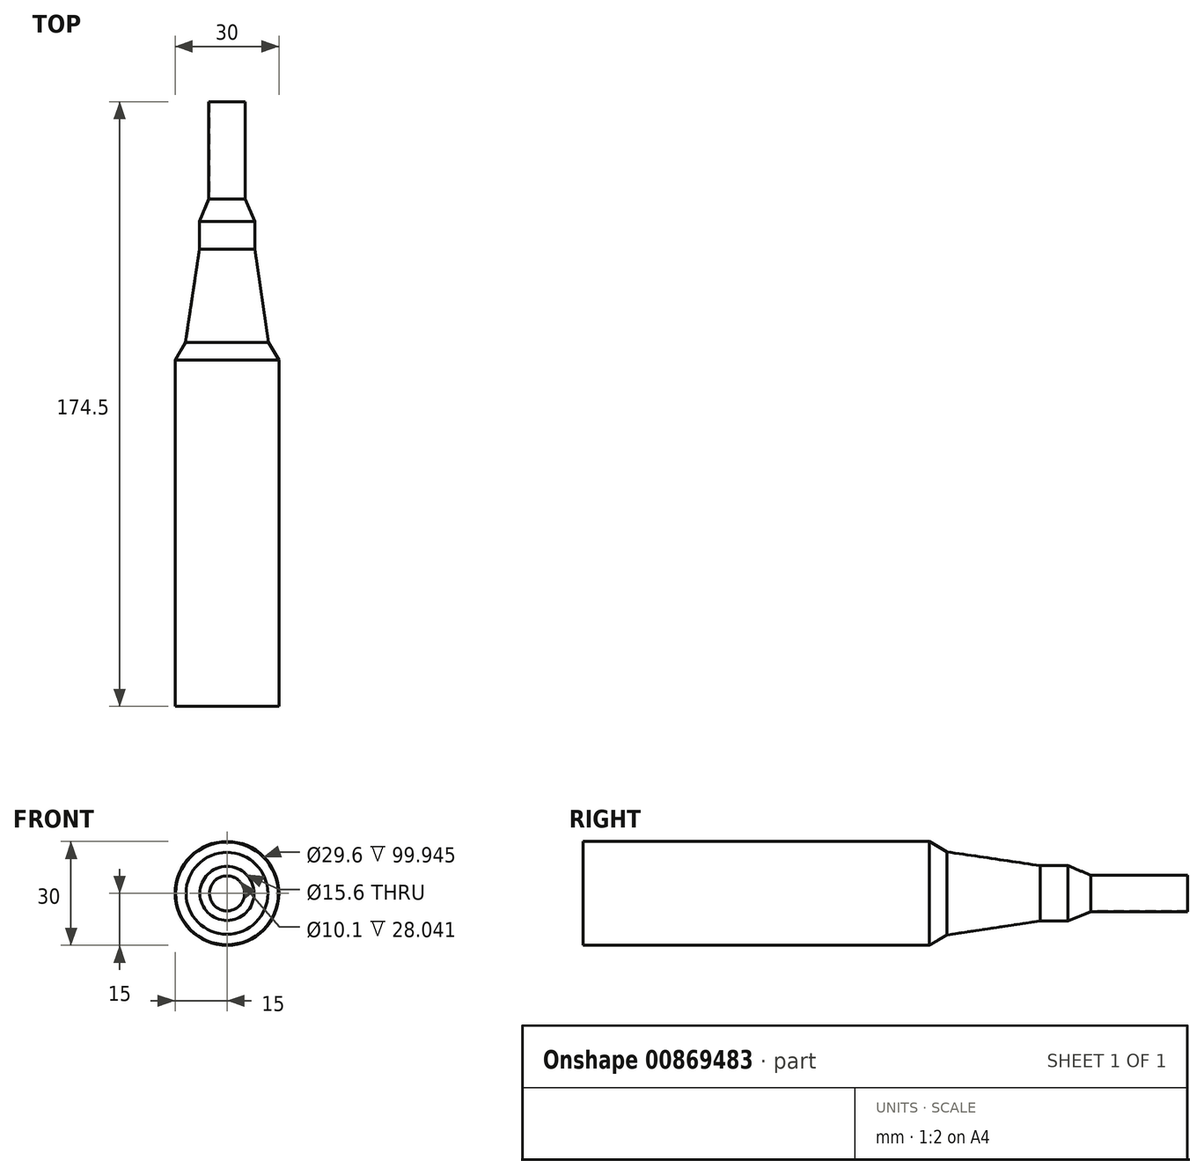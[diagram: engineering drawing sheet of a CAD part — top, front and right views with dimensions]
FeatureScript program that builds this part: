
annotation { "Feature Type Name" : "Feature", "Feature Type Description" : "" }
export const myFeature = defineFeature(function(context is Context, id is Id, definition is map)
    precondition{}
    {
        {
            var Q0;
            Q0=qCreatedBy(makeId("Front.planeOp"),FACE);
            var sketch = newSketch(context, id + "F0", { "sketchPlane" : qUnion([Q0])});
            skCircle(sketch, "E0", {"center": v(0, 0) * mm, "radius": 15 * mm});
            skSolve(sketch);
        }
        {
            var Q0;
            Q0=makeQuery(id+"F0.imprint","IMPRINT",FACE,{"disambiguationData":[TD([[makeQuery(id+"F0.imprint","IMPRINT",EDGE,{"derivedFrom":sQuery(id+"F0.wireOp",EDGE,"E0")}),1.0]])]});
            extrude(context, id + "F1", {"entities" : qUnion([Q0]), "oppositeDirection" : true, "depth" : 100 * mm, "offsetDistance" : 25 * mm});
        }
        {
            var Q0;
            Q0=makeQuery(id+"F1.opExtrude","CAP_FACE",FACE,{"disambiguationData":[OSD([sQuery(id+"F0.wireOp",EDGE,"E0")])],"isStart":false});
            cPlane(context, id + "F2", {"entities" : qUnion([Q0]), "cplaneType" : CPlaneType.OFFSET, "offset" : 5 * mm, "width" : 150 * mm, "height" : 150 * mm});
        }
        {
            var Q0;
            Q0=qCreatedBy(id+"F2.planeOp",FACE);
            var sketch = newSketch(context, id + "F3", { "sketchPlane" : qUnion([Q0])});
            skPoint(sketch, "E1.0", {"position": v(0, 0) * mm});
            skCircle(sketch, "E2", {"center": v(0, 0) * mm, "radius": 12 * mm});
            skSolve(sketch);
        }
        {
            var Q1;
            Q1=makeQuery(id+"F1.opExtrude","CAP_FACE",FACE,{"disambiguationData":[OSD([sQuery(id+"F0.wireOp",EDGE,"E0")])],"isStart":false});
            var Q2;
            Q2=makeQuery(id+"F3.imprint","IMPRINT",FACE,{"disambiguationData":[TD([[makeQuery(id+"F3.imprint","IMPRINT",EDGE,{"derivedFrom":sQuery(id+"F3.wireOp",EDGE,"E2")}),1.0]])]});
            loft(context, id + "F4", {"operationType" : NewBodyOperationType.ADD, "sheetProfilesArray" : [{ "sheetProfileEntities" : qUnion([Q1]) }, { "sheetProfileEntities" : qUnion([Q2]) }]});
        }
        {
            var Q0;
            Q0=makeQuery(id+"F4.opLoft","CAP_FACE",FACE,{"disambiguationData":[OSD([makeQuery(id+"F3.imprint","IMPRINT",FACE,{"disambiguationData":[TD([[makeQuery(id+"F3.imprint","IMPRINT",EDGE,{"derivedFrom":sQuery(id+"F3.wireOp",EDGE,"E2")}),1.0]])]})])],"isStart":true});
            cPlane(context, id + "F5", {"entities" : qUnion([Q0]), "cplaneType" : CPlaneType.OFFSET, "offset" : 27 * mm, "width" : 150 * mm, "height" : 150 * mm});
        }
        {
            var Q0;
            Q0=qCreatedBy(id+"F5.planeOp",FACE);
            var sketch = newSketch(context, id + "F6", { "sketchPlane" : qUnion([Q0])});
            skPoint(sketch, "E3.0", {"position": v(0, 0) * mm});
            skCircle(sketch, "E4", {"center": v(0, 0) * mm, "radius": 8 * mm});
            skSolve(sketch);
        }
        {
            var Q1;
            Q1=makeQuery(id+"F6.imprint","IMPRINT",FACE,{"disambiguationData":[TD([[makeQuery(id+"F6.imprint","IMPRINT",EDGE,{"derivedFrom":sQuery(id+"F6.wireOp",EDGE,"E4")}),1.0]])]});
            var Q2;
            Q2=makeQuery(id+"F4.opLoft","CAP_FACE",FACE,{"disambiguationData":[OSD([makeQuery(id+"F3.imprint","IMPRINT",FACE,{"disambiguationData":[TD([[makeQuery(id+"F3.imprint","IMPRINT",EDGE,{"derivedFrom":sQuery(id+"F3.wireOp",EDGE,"E2")}),1.0]])]})])],"isStart":true});
            loft(context, id + "F7", {"operationType" : NewBodyOperationType.ADD, "sheetProfilesArray" : [{ "sheetProfileEntities" : qUnion([Q1]) }, { "sheetProfileEntities" : qUnion([Q2]) }]});
        }
        {
            var Q0;
            Q0=makeQuery(id+"F7.opLoft","CAP_FACE",FACE,{"disambiguationData":[OSD([makeQuery(id+"F6.imprint","IMPRINT",FACE,{"disambiguationData":[TD([[makeQuery(id+"F6.imprint","IMPRINT",EDGE,{"derivedFrom":sQuery(id+"F6.wireOp",EDGE,"E4")}),1.0]])]})])],"isStart":true});
            extrude(context, id + "F8", {"entities" : qUnion([Q0]), "operationType" : NewBodyOperationType.ADD, "depth" : 8 * mm, "offsetDistance" : 25 * mm});
        }
        {
            var Q0;
            Q0=makeQuery(id+"F8.opExtrude","CAP_FACE",FACE,{"disambiguationData":[OSD([makeQuery(id+"F6.imprint","IMPRINT",FACE,{"disambiguationData":[TD([[makeQuery(id+"F6.imprint","IMPRINT",EDGE,{"derivedFrom":sQuery(id+"F6.wireOp",EDGE,"E4")}),1.0]])]})])],"isStart":false});
            cPlane(context, id + "F9", {"entities" : qUnion([Q0]), "cplaneType" : CPlaneType.OFFSET, "offset" : 6.5 * mm, "width" : 150 * mm, "height" : 150 * mm});
        }
        {
            var Q0;
            Q0=qCreatedBy(id+"F9.planeOp",FACE);
            var sketch = newSketch(context, id + "F10", { "sketchPlane" : qUnion([Q0])});
            skPoint(sketch, "E5.0", {"position": v(0, 0) * mm});
            skCircle(sketch, "E6", {"center": v(0, 0) * mm, "radius": 5.25 * mm});
            skSolve(sketch);
        }
        {
            var Q1;
            Q1=makeQuery(id+"F8.opExtrude","CAP_FACE",FACE,{"disambiguationData":[OSD([makeQuery(id+"F6.imprint","IMPRINT",FACE,{"disambiguationData":[TD([[makeQuery(id+"F6.imprint","IMPRINT",EDGE,{"derivedFrom":sQuery(id+"F6.wireOp",EDGE,"E4")}),1.0]])]})])],"isStart":false});
            var Q2;
            Q2=makeQuery(id+"F10.imprint","IMPRINT",FACE,{"disambiguationData":[TD([[makeQuery(id+"F10.imprint","IMPRINT",EDGE,{"derivedFrom":sQuery(id+"F10.wireOp",EDGE,"E6")}),1.0]])]});
            loft(context, id + "F11", {"operationType" : NewBodyOperationType.ADD, "sheetProfilesArray" : [{ "sheetProfileEntities" : qUnion([Q1]) }, { "sheetProfileEntities" : qUnion([Q2]) }]});
        }
        {
            var Q0;
            Q0=makeQuery(id+"F11.opLoft","CAP_FACE",FACE,{"disambiguationData":[OSD([makeQuery(id+"F10.imprint","IMPRINT",FACE,{"disambiguationData":[TD([[makeQuery(id+"F10.imprint","IMPRINT",EDGE,{"derivedFrom":sQuery(id+"F10.wireOp",EDGE,"E6")}),1.0]])]})])],"isStart":true});
            extrude(context, id + "F12", {"entities" : qUnion([Q0]), "operationType" : NewBodyOperationType.ADD, "depth" : 28 * mm, "offsetDistance" : 25 * mm});
        }
        {
            var Q0;
            Q0=makeQuery(id+"F1.opExtrude","CAP_FACE",FACE,{"disambiguationData":[OSD([sQuery(id+"F0.wireOp",EDGE,"E0")])],"isStart":true});
            var Q1;
            Q1=makeQuery(id+"F12.opExtrude","CAP_FACE",FACE,{"disambiguationData":[OSD([makeQuery(id+"F10.imprint","IMPRINT",FACE,{"disambiguationData":[TD([[makeQuery(id+"F10.imprint","IMPRINT",EDGE,{"derivedFrom":sQuery(id+"F10.wireOp",EDGE,"E6")}),1.0]])]})])],"isStart":false});
            shell(context, id + "F13", {"entities" : qUnion([Q0, Q1]), "thickness" : 0.2 * mm});
        }
    });
